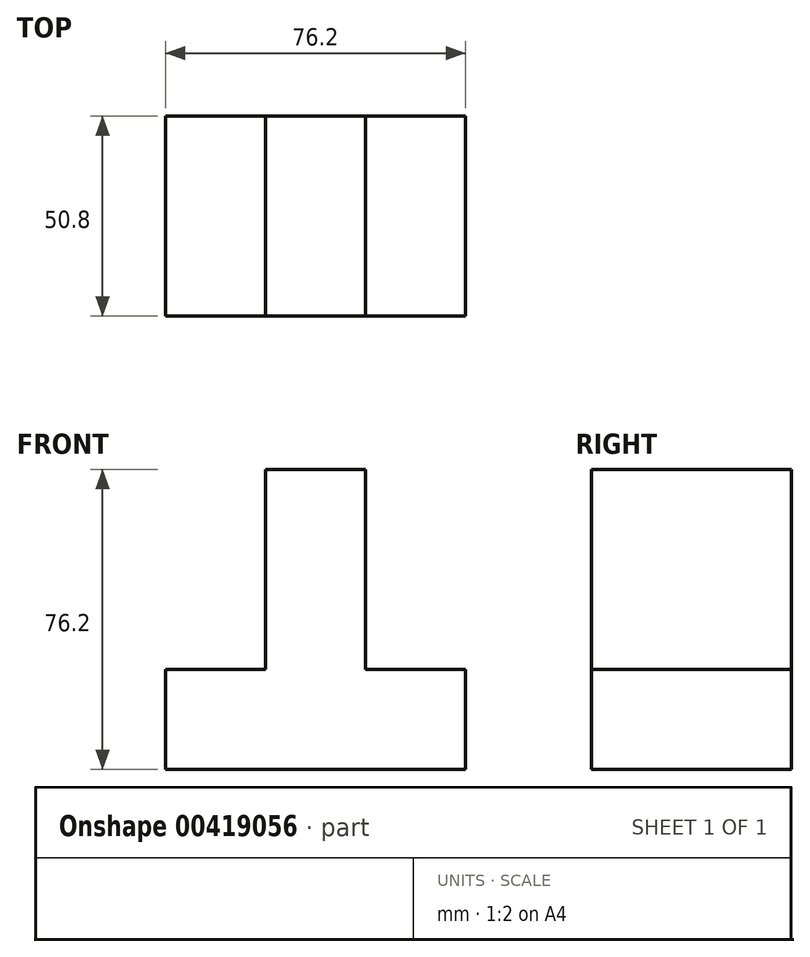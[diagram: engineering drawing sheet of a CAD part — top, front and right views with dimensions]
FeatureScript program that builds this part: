
annotation { "Feature Type Name" : "Feature", "Feature Type Description" : "" }
export const myFeature = defineFeature(function(context is Context, id is Id, definition is map)
    precondition{}
    {
        {
            var Q0;
            Q0=qCreatedBy(makeId("Front.planeOp"),FACE);
            var sketch = newSketch(context, id + "F0", { "sketchPlane" : qUnion([Q0])});
            skLineSegment(sketch, "E0", {"start": v(0, 0) * mm, "end": v(-76.2, 0) * mm});
            skLineSegment(sketch, "E1", {"start": v(-76.2, 0) * mm, "end": v(-76.2, 25.4) * mm});
            skLineSegment(sketch, "E2", {"start": v(-76.2, 25.4) * mm, "end": v(-50.8, 25.4) * mm});
            skLineSegment(sketch, "E3", {"start": v(0, 0) * mm, "end": v(0, 25.4) * mm});
            skLineSegment(sketch, "E4", {"start": v(0, 25.4) * mm, "end": v(-25.4, 25.4) * mm});
            skLineSegment(sketch, "E5", {"start": v(-50.8, 25.4) * mm, "end": v(-50.8, 76.2) * mm});
            skLineSegment(sketch, "E6", {"start": v(-25.4, 25.4) * mm, "end": v(-25.4, 76.2) * mm});
            skLineSegment(sketch, "E7", {"start": v(-25.4, 76.2) * mm, "end": v(-50.8, 76.2) * mm});
            skSolve(sketch);
        }
        {
            var Q0;
            Q0 = qSketchRegion(id + "F0", true);
            extrude(context, id + "F1", {"entities" : qUnion([Q0]), "depth" : 50.8 * mm});
        }
    });
